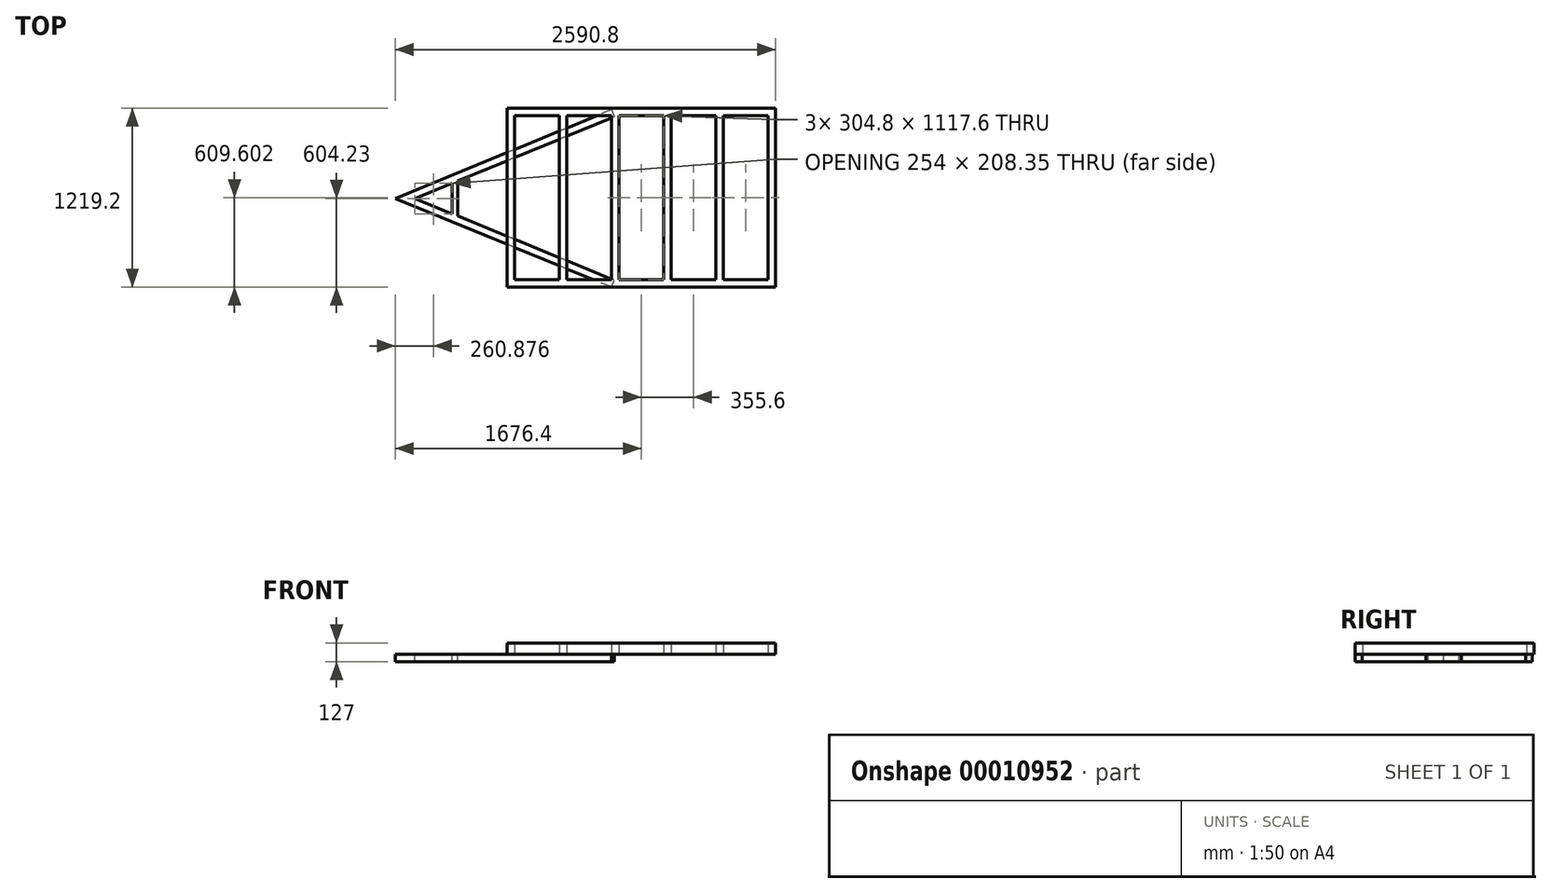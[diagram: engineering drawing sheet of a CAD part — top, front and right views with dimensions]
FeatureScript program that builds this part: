
annotation { "Feature Type Name" : "Feature", "Feature Type Description" : "" }
export const myFeature = defineFeature(function(context is Context, id is Id, definition is map)
    precondition{}
    {
        {
            var Q0;
            Q0=qCreatedBy(makeId("Top.planeOp"),FACE);
            var sketch = newSketch(context, id + "F0", { "sketchPlane" : qUnion([Q0])});
            skLineSegment(sketch, "E0.bottom", {"start": v(386.23, 614.97) * mm, "end": v(-1442.57, 614.97) * mm});
            skLineSegment(sketch, "E0.top", {"start": v(386.23, -604.23) * mm, "end": v(-1442.57, -604.23) * mm});
            skLineSegment(sketch, "E0.left", {"start": v(386.23, 614.97) * mm, "end": v(386.23, -604.23) * mm});
            skLineSegment(sketch, "E0.right", {"start": v(-1442.57, 614.97) * mm, "end": v(-1442.57, -604.23) * mm});
            skLineSegment(sketch, "E1.0", {"start": v(-1391.77, 564.17) * mm, "end": v(-1391.77, -553.43) * mm});
            skLineSegment(sketch, "E2.left", {"start": v(-1086.97, 564.17) * mm, "end": v(-1086.97, -553.43) * mm});
            skLineSegment(sketch, "E3.trimOffspring", {"start": v(-1086.97, 564.17) * mm, "end": v(-1391.77, 564.17) * mm});
            skLineSegment(sketch, "E4.trimOffspring", {"start": v(-1086.97, -553.43) * mm, "end": v(-1391.77, -553.43) * mm});
            skLineSegment(sketch, "E5.1.0.0", {"start": v(-731.37, 564.17) * mm, "end": v(-731.37, -553.43) * mm});
            skLineSegment(sketch, "E5.1.0.1", {"start": v(-731.37, 564.17) * mm, "end": v(-1036.17, 564.17) * mm});
            skLineSegment(sketch, "E5.1.0.2", {"start": v(-1036.17, 564.17) * mm, "end": v(-1036.17, -553.43) * mm});
            skLineSegment(sketch, "E5.1.0.3", {"start": v(-731.37, -553.43) * mm, "end": v(-1036.17, -553.43) * mm});
            skLineSegment(sketch, "E5.2.0.0", {"start": v(-375.77, 564.17) * mm, "end": v(-375.77, -553.43) * mm});
            skLineSegment(sketch, "E5.2.0.1", {"start": v(-375.77, 564.17) * mm, "end": v(-680.57, 564.17) * mm});
            skLineSegment(sketch, "E5.2.0.2", {"start": v(-680.57, 564.17) * mm, "end": v(-680.57, -553.43) * mm});
            skLineSegment(sketch, "E5.2.0.3", {"start": v(-375.77, -553.43) * mm, "end": v(-680.57, -553.43) * mm});
            skLineSegment(sketch, "E5.3.0.0", {"start": v(-20.17, 564.17) * mm, "end": v(-20.17, -553.43) * mm});
            skLineSegment(sketch, "E5.3.0.1", {"start": v(-20.17, 564.17) * mm, "end": v(-324.97, 564.17) * mm});
            skLineSegment(sketch, "E5.3.0.2", {"start": v(-324.97, 564.17) * mm, "end": v(-324.97, -553.43) * mm});
            skLineSegment(sketch, "E5.3.0.3", {"start": v(-20.17, -553.43) * mm, "end": v(-324.97, -553.43) * mm});
            skLineSegment(sketch, "E5.4.0.0", {"start": v(335.43, 564.17) * mm, "end": v(335.43, -553.43) * mm});
            skLineSegment(sketch, "E5.4.0.1", {"start": v(335.43, 564.17) * mm, "end": v(30.63, 564.17) * mm});
            skLineSegment(sketch, "E5.4.0.2", {"start": v(30.63, 564.17) * mm, "end": v(30.63, -553.43) * mm});
            skLineSegment(sketch, "E5.4.0.3", {"start": v(335.43, -553.43) * mm, "end": v(30.63, -553.43) * mm});
            skLineSegment(sketch, "E5.direction1", {"start": v(-1086.97, -553.43) * mm, "end": v(-731.37, -553.43) * mm, "construction": true});
            skSolve(sketch);
        }
        {
            var Q0;
            Q0 = qSketchRegion(id + "F0", true);
            extrude(context, id + "F1", {"entities" : qUnion([Q0]), "depth" : 76.2 * mm});
        }
        {
            var Q0;
            Q0=makeQuery(id+"F1.opExtrude","CAP_FACE",FACE,{"disambiguationData":[OSD([sQuery(id+"F0.wireOp",EDGE,"E0.bottom"),sQuery(id+"F0.wireOp",EDGE,"E0.top"),sQuery(id+"F0.wireOp",EDGE,"E0.left"),sQuery(id+"F0.wireOp",EDGE,"E0.right"),sQuery(id+"F0.wireOp",EDGE,"E1.0"),sQuery(id+"F0.wireOp",EDGE,"E2.left"),sQuery(id+"F0.wireOp",EDGE,"E3.trimOffspring"),sQuery(id+"F0.wireOp",EDGE,"E4.trimOffspring"),sQuery(id+"F0.wireOp",EDGE,"E5.1.0.0"),sQuery(id+"F0.wireOp",EDGE,"E5.1.0.1"),sQuery(id+"F0.wireOp",EDGE,"E5.1.0.2"),sQuery(id+"F0.wireOp",EDGE,"E5.1.0.3"),sQuery(id+"F0.wireOp",EDGE,"E5.2.0.0"),sQuery(id+"F0.wireOp",EDGE,"E5.2.0.1"),sQuery(id+"F0.wireOp",EDGE,"E5.2.0.2"),sQuery(id+"F0.wireOp",EDGE,"E5.2.0.3"),sQuery(id+"F0.wireOp",EDGE,"E5.3.0.0"),sQuery(id+"F0.wireOp",EDGE,"E5.3.0.1"),sQuery(id+"F0.wireOp",EDGE,"E5.3.0.2"),sQuery(id+"F0.wireOp",EDGE,"E5.3.0.3"),sQuery(id+"F0.wireOp",EDGE,"E5.4.0.0"),sQuery(id+"F0.wireOp",EDGE,"E5.4.0.1"),sQuery(id+"F0.wireOp",EDGE,"E5.4.0.2"),sQuery(id+"F0.wireOp",EDGE,"E5.4.0.3")])],"isStart":true});
            var sketch = newSketch(context, id + "F2", { "sketchPlane" : qUnion([Q0])});
            skLineSegment(sketch, "E6", {"start": v(-731.37, 604.23) * mm, "end": v(-2204.57, 0) * mm});
            skLineSegment(sketch, "E7.0", {"start": v(-712.09, 557.23) * mm, "end": v(-1778.6, 119.8) * mm});
            skLineSegment(sketch, "E8", {"start": v(-731.37, 604.23) * mm, "end": v(-712.09, 557.23) * mm});
            skLineSegment(sketch, "E9", {"start": v(386.23, 0) * mm, "end": v(-2619.5, 0) * mm, "construction": true});
            skLineSegment(sketch, "E10.0.MirrorCS", {"start": v(-731.37, -604.23) * mm, "end": v(-712.09, -557.23) * mm});
            skLineSegment(sketch, "E10.1.MirrorCS", {"start": v(-712.09, -557.23) * mm, "end": v(-1778.6, -119.8) * mm});
            skLineSegment(sketch, "E10.2.MirrorCS", {"start": v(-731.37, -604.23) * mm, "end": v(-2204.57, 0) * mm});
            skPoint(sketch, "E11.orphan", {"position": v(-2185.29, 47) * mm});
            skPoint(sketch, "E12.orphan", {"position": v(-2185.29, -47) * mm});
            skLineSegment(sketch, "E13.left", {"start": v(-1816.7, 104.18) * mm, "end": v(-1816.7, -104.18) * mm});
            skLineSegment(sketch, "E13.right", {"start": v(-1778.6, 119.8) * mm, "end": v(-1778.6, -119.8) * mm});
            skLineSegment(sketch, "E14.trimOffspring", {"start": v(-1816.7, -104.18) * mm, "end": v(-2070.7, 0) * mm});
            skLineSegment(sketch, "E15.trimOffspring", {"start": v(-1816.7, 104.18) * mm, "end": v(-2070.7, 0) * mm});
            skSolve(sketch);
        }
        {
            var Q0;
            Q0 = qSketchRegion(id + "F2", true);
            extrude(context, id + "F3", {"entities" : qUnion([Q0]), "operationType" : NewBodyOperationType.ADD, "depth" : 50.8 * mm});
        }
    });
